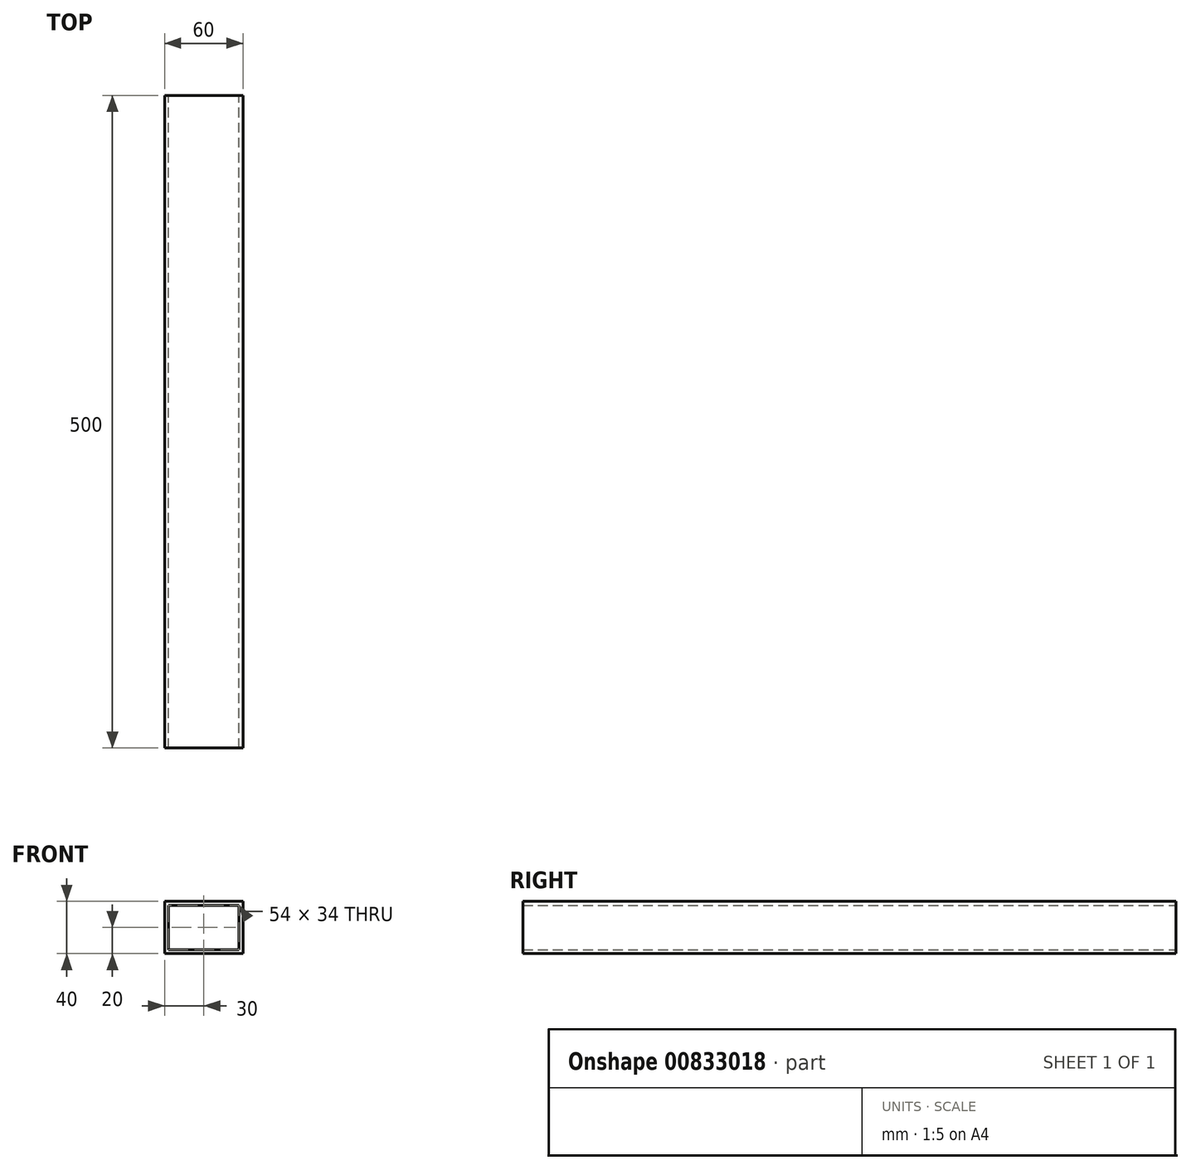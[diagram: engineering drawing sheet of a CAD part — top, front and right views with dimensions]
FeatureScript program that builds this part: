
annotation { "Feature Type Name" : "Feature", "Feature Type Description" : "" }
export const myFeature = defineFeature(function(context is Context, id is Id, definition is map)
    precondition{}
    {
        {
            var Q0;
            Q0=qCreatedBy(makeId("Front.planeOp"),FACE);
            var sketch = newSketch(context, id + "F0", { "sketchPlane" : qUnion([Q0])});
            skLineSegment(sketch, "E0.bottom", {"start": v(-30, 20) * mm, "end": v(30, 20) * mm});
            skLineSegment(sketch, "E0.top", {"start": v(-30, -20) * mm, "end": v(30, -20) * mm});
            skLineSegment(sketch, "E0.left", {"start": v(-30, 20) * mm, "end": v(-30, -20) * mm});
            skLineSegment(sketch, "E0.right", {"start": v(30, 20) * mm, "end": v(30, -20) * mm});
            skPoint(sketch, "E0.middle", {"position": v(0, 0) * mm});
            skLineSegment(sketch, "E1.bottom", {"start": v(-27, 17) * mm, "end": v(27, 17) * mm});
            skLineSegment(sketch, "E1.top", {"start": v(-27, -17) * mm, "end": v(27, -17) * mm});
            skLineSegment(sketch, "E1.left", {"start": v(-27, 17) * mm, "end": v(-27, -17) * mm});
            skLineSegment(sketch, "E1.right", {"start": v(27, 17) * mm, "end": v(27, -17) * mm});
            skSolve(sketch);
        }
        {
            var Q0;
            Q0=makeQuery(id+"F0.imprint","IMPRINT",FACE,{"disambiguationData":[TD([[makeQuery(id+"F0.imprint","IMPRINT",EDGE,{"derivedFrom":sQuery(id+"F0.wireOp",EDGE,"E0.bottom")}),-1.0]])]});
            extrude(context, id + "F1", {"entities" : qUnion([Q0]), "endBound" : BoundingType.SYMMETRIC, "depth" : 500 * mm, "offsetDistance" : 25 * mm});
        }
    });
